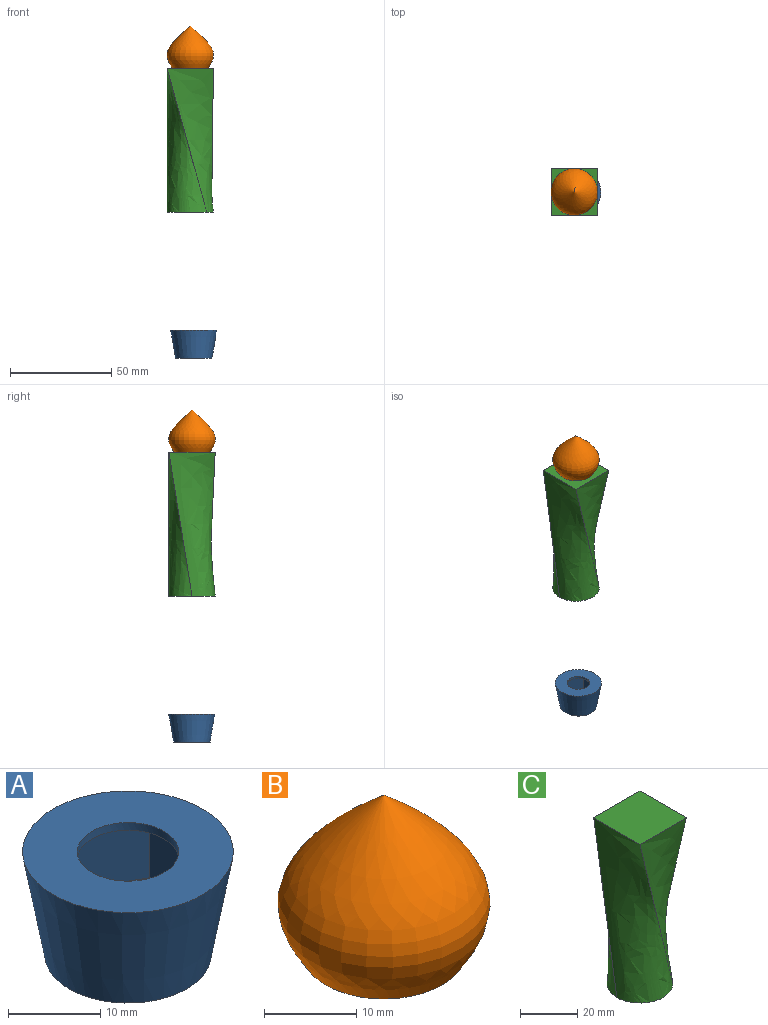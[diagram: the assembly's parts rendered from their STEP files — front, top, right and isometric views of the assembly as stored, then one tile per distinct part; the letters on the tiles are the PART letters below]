
ASSEMBLY  parts=3 mates=1
PART A: 13 faces, bbox 22.9x22.9x13.7 mm
  f0: cylinder r=5.5mm len=11mm, axis (0,0,-1), area 145.1mm2, adj f1,f5
  f1: plane 18x18mm, normal (0,0,-1), area 159.4mm2, adj f0,f2
  f2: cone r=11.43mm half-angle=10deg, axis (0,0,1), area 894mm2, adj f1,f3
  f3: plane 22.86x22.86mm, normal (0,0,1), area 315.4mm2, adj f2,f4
  f4: cylinder r=5.5mm len=11mm, axis (0,0,-1), area 35.1mm2, adj f3,f6
  f5: plane 17.78x15.4mm, normal (0,0,1), area 110.3mm2, adj f0,f7,f8,f9,f10,f11,f12
  f6: plane 17.78x15.4mm, normal (0,0,-1), area 110.3mm2, adj f4,f7,f8,f9,f10,f11,f12
  f7: plane 8.5x7.7mm, normal (-0.5,-0.87,0), area 75.6mm2, adj f5,f6,f8,f12
  f8: plane 8.5x7.7mm, normal (0.5,-0.87,0), area 75.6mm2, adj f5,f6,f7,f9
  f9: plane 8.89x8.5mm, normal (1,0,0), area 75.6mm2, adj f5,f6,f8,f10
  f10: plane 8.5x7.7mm, normal (0.5,0.87,0), area 75.6mm2, adj f5,f6,f9,f11
  f11: plane 8.5x7.7mm, normal (-0.5,0.87,0), area 75.6mm2, adj f5,f6,f10,f12
  f12: plane 8.89x8.5mm, normal (-1,0,0), area 75.6mm2, adj f5,f6,f7,f11
PART B: 2 faces, bbox 23.1x23.1x20.8 mm
  f0: plane 17.78x17.78mm, normal (0,0,-1), area 248.3mm2, adj f1
  f1: revolved ~23.08x23.08mm, area 1255.5mm2, adj f0
PART C: 8 faces, bbox 22.9x22.9x71.1 mm
  f0: plane 22.88x22.87mm, normal (0,0,-1), area 315.4mm2, adj f2,f3,f4,f5,f6
  f1: plane 22.86x22.86mm, normal (0,0,1), area 522.6mm2, adj f2,f3,f4,f5
  f2: bspline ~71.12x22.92mm, area 1112mm2, adj f0,f1,f3,f5
  f3: bspline ~71.12x22.87mm, area 1190.4mm2, adj f0,f1,f2,f4
  f4: bspline ~71.12x22.86mm, area 1356.2mm2, adj f0,f1,f3,f5
  f5: bspline ~71.12x22.92mm, area 1536mm2, adj f0,f1,f2,f4
  f6: cylinder r=5.5mm len=25.4mm, axis (0,0,-1), area 877.8mm2, adj f0,f7
  f7: plane 11x11mm, normal (0,0,-1), area 95mm2, adj f6
PLACE A t=(-45.03,-49.29,-2.09)mm
PLACE B t=(-124.88,-79.58,189.81)mm
PLACE C t=(-124.88,-49.38,20.05)mm
MATE fastened B.f0 <-> C.f6  axis (0,0,-1) through (-124.88,-49.38,141.17)mm
